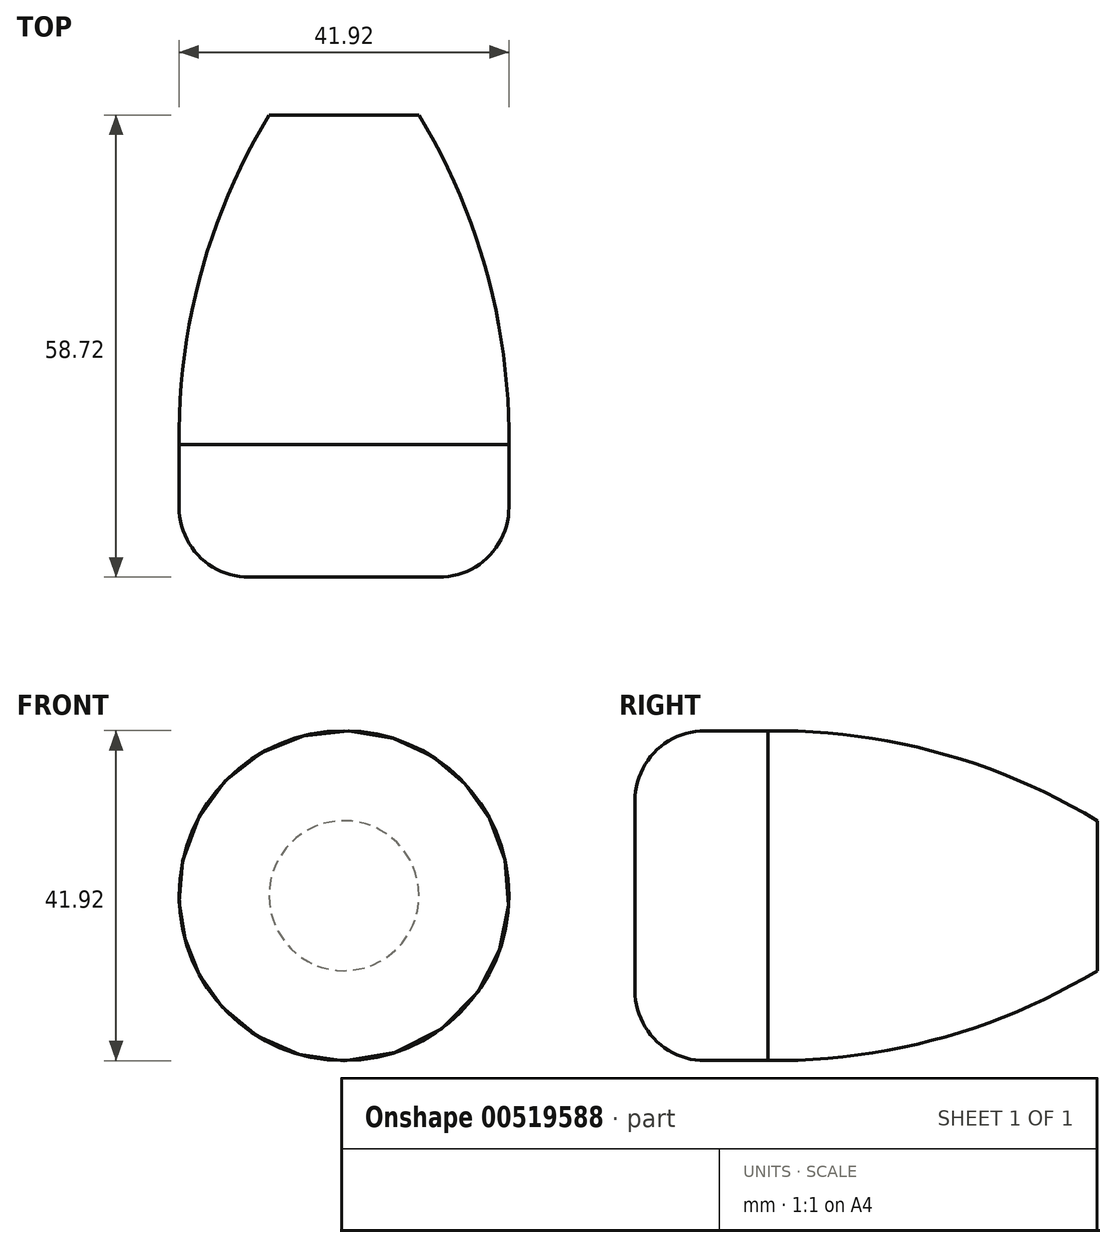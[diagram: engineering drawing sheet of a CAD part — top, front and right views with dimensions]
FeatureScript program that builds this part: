
annotation { "Feature Type Name" : "Feature", "Feature Type Description" : "" }
export const myFeature = defineFeature(function(context is Context, id is Id, definition is map)
    precondition{}
    {
        {
            var Q0;
            Q0=qCreatedBy(makeId("Right.planeOp"),FACE);
            var sketch = newSketch(context, id + "F0", { "sketchPlane" : qUnion([Q0])});
            skLineSegment(sketch, "E0", {"start": v(0, 0) * mm, "end": v(0, 12.06) * mm});
            skArc(sketch, "E1", {"start": v(58.72, 9.52) * mm, "mid": v(38.6, 18.16) * mm, "end": v(16.86, 20.95) * mm});
            skLineSegment(sketch, "E2", {"start": v(58.72, 9.52) * mm, "end": v(58.72, 0) * mm});
            skLineSegment(sketch, "E3", {"start": v(0, 0) * mm, "end": v(58.72, 0) * mm});
            skLineSegment(sketch, "E4", {"start": v(16.86, 20.95) * mm, "end": v(8.9, 20.95) * mm});
            skPoint(sketch, "E5.visualSharp", {"position": v(0, 20.95) * mm});
            skArc(sketch, "E5.filletArc", {"start": v(8.9, 20.95) * mm, "mid": v(2.6, 18.35) * mm, "end": v(0, 12.06) * mm});
            skSolve(sketch);
        }
        {
            var Q0;
            Q0 = qSketchRegion(id + "F0", true);
            var Q1;
            Q1=sQuery(id+"F0.wireOp",EDGE,"E3");
            revolve(context, id + "F1", {"entities" : qUnion([Q0]), "axis" : qUnion([Q1]), "revolveType" : RevolveType.FULL});
        }
    });
